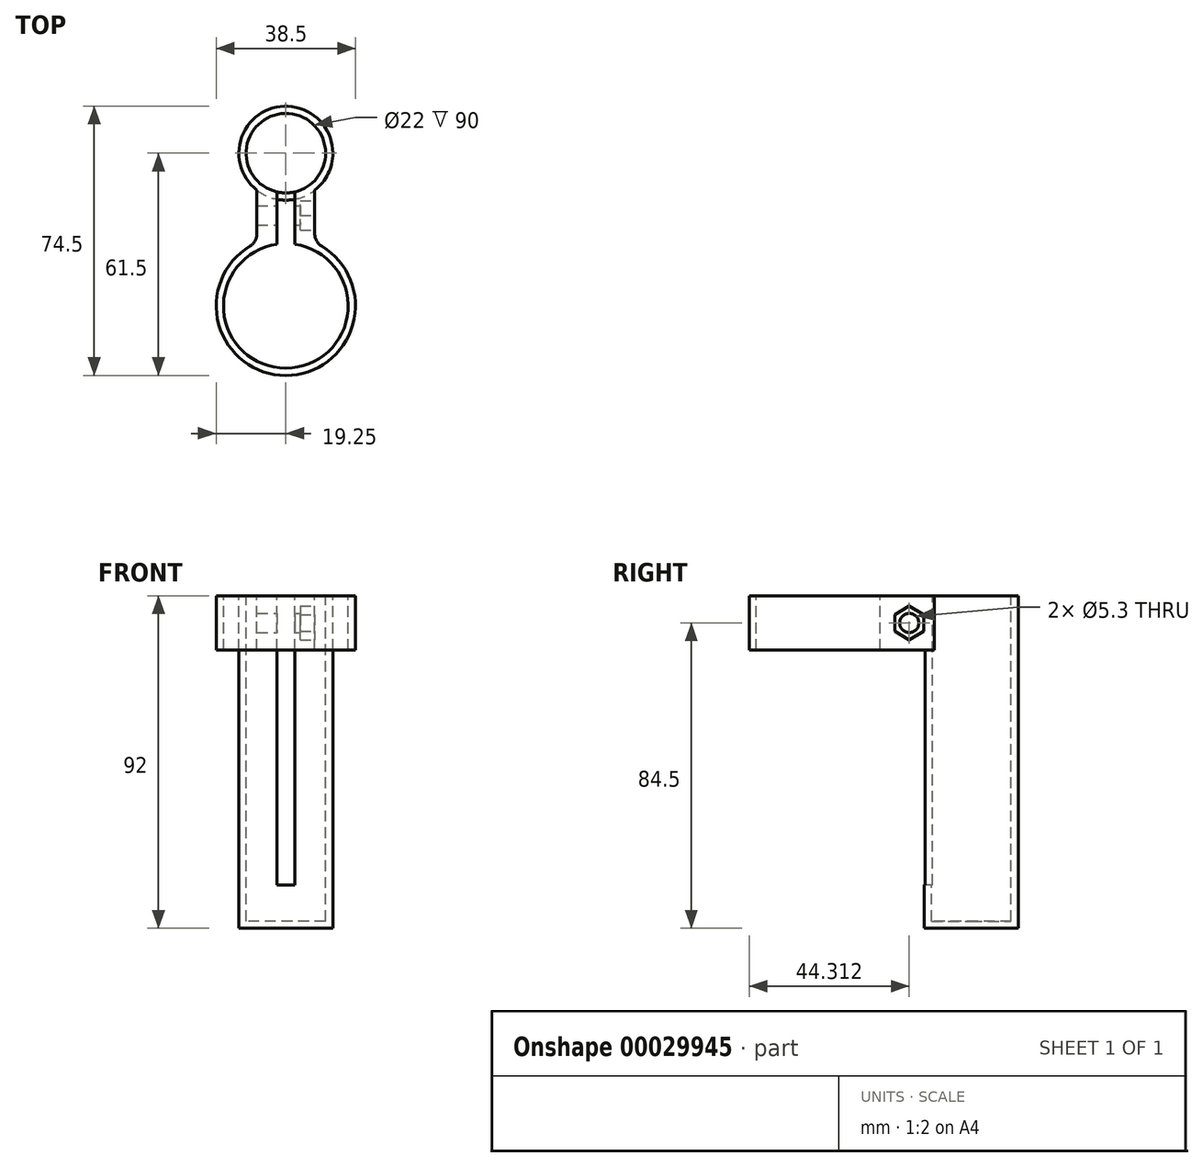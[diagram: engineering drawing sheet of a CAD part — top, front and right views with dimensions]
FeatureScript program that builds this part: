
annotation { "Feature Type Name" : "Feature", "Feature Type Description" : "" }
export const myFeature = defineFeature(function(context is Context, id is Id, definition is map)
    precondition{}
    {
        {
            var Q0;
            Q0=qCreatedBy(makeId("Top.planeOp"),FACE);
            var sketch = newSketch(context, id + "F0", { "sketchPlane" : qUnion([Q0])});
            skCircle(sketch, "E0", {"center": v(0, 0) * mm, "radius": 17.25 * mm});
            skCircle(sketch, "E1", {"center": v(0, 42.25) * mm, "radius": 11 * mm});
            skCircle(sketch, "E2", {"center": v(0, 42.25) * mm, "radius": 13 * mm});
            skCircle(sketch, "E3", {"center": v(0, 0) * mm, "radius": 19.25 * mm});
            skLineSegment(sketch, "E4", {"start": v(2.5, 31.54) * mm, "end": v(2.5, 17.07) * mm});
            skLineSegment(sketch, "E5", {"start": v(-2.5, 31.54) * mm, "end": v(-2.5, 17.07) * mm});
            skLineSegment(sketch, "E6", {"start": v(-8, 17.5) * mm, "end": v(-8, 32) * mm});
            skLineSegment(sketch, "E7", {"start": v(8, 32) * mm, "end": v(8, 17.5) * mm});
            skSolve(sketch);
        }
        {
            var Q0;
            {var subQ0=sQuery(id+"F0.wireOp",EDGE,"E6");Q0=makeQuery(id+"F0.imprint","IMPRINT",FACE,{"disambiguationData":[TD([[makeQuery(id+"F0.imprint","IMPRINT",EDGE,{"derivedFrom":subQ0}),-1.0]])]});}
            var Q1;
            {var subQ0=sQuery(id+"F0.wireOp",EDGE,"E7");Q1=makeQuery(id+"F0.imprint","IMPRINT",FACE,{"disambiguationData":[TD([[makeQuery(id+"F0.imprint","IMPRINT",EDGE,{"derivedFrom":subQ0}),-1.0]])]});}
            var Q2;
            {var subQ0=sQuery(id+"F0.wireOp",EDGE,"E6");Q2=makeQuery(id+"F0.imprint","IMPRINT",FACE,{"disambiguationData":[TD([[makeQuery(id+"F0.imprint","IMPRINT",EDGE,{"derivedFrom":subQ0}),-1.0]])]});}
            var Q3;
            {var subQ0=sQuery(id+"F0.wireOp",EDGE,"E7");Q3=makeQuery(id+"F0.imprint","IMPRINT",FACE,{"disambiguationData":[TD([[makeQuery(id+"F0.imprint","IMPRINT",EDGE,{"derivedFrom":subQ0}),-1.0]])]});}
            var Q4;
            {var subQ0=sQuery(id+"F0.wireOp",EDGE,"E4");var subQ3=sQuery(id+"F0.wireOp",EDGE,"E0");var subQ4=makeQuery(id+"F0.imprint","INTERSECT",VERTEX,{"derivedFrom":[subQ3,subQ0]});Q4=makeQuery(id+"F0.imprint","IMPRINT",FACE,{"disambiguationData":[TD([[makeQuery(id+"F0.imprint","IMPRINT",EDGE,{"disambiguationData":[TD([[subQ4,1.0]])],"derivedFrom":subQ3}),-1.0]])]});}
            var Q5;
            {var subQ0=sQuery(id+"F0.wireOp",EDGE,"E6");Q5=makeQuery(id+"F0.imprint","IMPRINT",FACE,{"disambiguationData":[TD([[makeQuery(id+"F0.imprint","IMPRINT",EDGE,{"derivedFrom":subQ0}),-1.0]])]});}
            var Q6;
            {var subQ0=sQuery(id+"F0.wireOp",EDGE,"E7");Q6=makeQuery(id+"F0.imprint","IMPRINT",FACE,{"disambiguationData":[TD([[makeQuery(id+"F0.imprint","IMPRINT",EDGE,{"derivedFrom":subQ0}),-1.0]])]});}
            var Q7;
            {var subQ0=sQuery(id+"F0.wireOp",EDGE,"E4");var subQ3=sQuery(id+"F0.wireOp",EDGE,"E0");var subQ4=makeQuery(id+"F0.imprint","INTERSECT",VERTEX,{"derivedFrom":[subQ3,subQ0]});Q7=makeQuery(id+"F0.imprint","IMPRINT",FACE,{"disambiguationData":[TD([[makeQuery(id+"F0.imprint","IMPRINT",EDGE,{"disambiguationData":[TD([[subQ4,1.0]])],"derivedFrom":subQ3}),-1.0]])]});}
            extrude(context, id + "F1", {"entities" : qUnion([Q0, Q1, Q2, Q3, Q4, Q5, Q6, Q7]), "oppositeDirection" : true, "depth" : 15 * mm});
        }
        {
            var Q0;
            {var subQ0=sQuery(id+"F0.wireOp",EDGE,"E5");var subQ3=sQuery(id+"F0.wireOp",EDGE,"E1");var subQ4=makeQuery(id+"F0.imprint","INTERSECT",VERTEX,{"derivedFrom":[subQ3,subQ0]});Q0=makeQuery(id+"F0.imprint","IMPRINT",FACE,{"disambiguationData":[TD([[makeQuery(id+"F0.imprint","IMPRINT",EDGE,{"disambiguationData":[TD([[subQ4,1.0]])],"derivedFrom":subQ3}),-1.0]])]});}
            var Q1;
            {var subQ0=sQuery(id+"F0.wireOp",EDGE,"E1");var subQ4=makeQuery(id+"F0.imprint","INTERSECT",VERTEX,{"derivedFrom":[subQ0,sQuery(id+"F0.wireOp",EDGE,"E5")]});Q1=makeQuery(id+"F0.imprint","IMPRINT",FACE,{"disambiguationData":[TD([[makeQuery(id+"F0.imprint","IMPRINT",EDGE,{"disambiguationData":[TD([[subQ4,1.0]])],"derivedFrom":subQ0}),1.0]])]});}
            var Q2;
            {var subQ3=sQuery(id+"F0.wireOp",EDGE,"E1");var subQ5=sQuery(id+"F0.wireOp",EDGE,"E4");var subQ7=makeQuery(id+"F0.imprint","INTERSECT",VERTEX,{"derivedFrom":[subQ3,subQ5]});Q2=makeQuery(id+"F0.imprint","IMPRINT",FACE,{"disambiguationData":[TD([[makeQuery(id+"F0.imprint","IMPRINT",EDGE,{"disambiguationData":[TD([[subQ7,1.0]])],"derivedFrom":subQ3}),-1.0]])]});}
            var Q3;
            {var subQ3=sQuery(id+"F0.wireOp",EDGE,"E1");var subQ5=sQuery(id+"F0.wireOp",EDGE,"b73e8383-4520-4388-ab81-a26b702ea739");var subQ7=makeQuery(id+"F0.imprint","INTERSECT",VERTEX,{"derivedFrom":[subQ3,subQ5]});Q3=makeQuery(id+"F0.imprint","IMPRINT",FACE,{"disambiguationData":[TD([[makeQuery(id+"F0.imprint","IMPRINT",EDGE,{"disambiguationData":[TD([[subQ7,1.0]])],"derivedFrom":subQ3}),-1.0]])]});}
            var Q4;
            {var subQ3=sQuery(id+"F0.wireOp",EDGE,"E1");var subQ5=sQuery(id+"F0.wireOp",EDGE,"E4");var subQ7=makeQuery(id+"F0.imprint","INTERSECT",VERTEX,{"derivedFrom":[subQ3,subQ5]});Q4=makeQuery(id+"F0.imprint","IMPRINT",FACE,{"disambiguationData":[TD([[makeQuery(id+"F0.imprint","IMPRINT",EDGE,{"disambiguationData":[TD([[subQ7,-1.0]])],"derivedFrom":subQ3}),-1.0]])]});}
            extrude(context, id + "F2", {"entities" : qUnion([Q0, Q1, Q2, Q3, Q4]), "operationType" : NewBodyOperationType.ADD, "oppositeDirection" : true, "depth" : 92 * mm});
        }
        {
            var Q0;
            {var subQ0=sQuery(id+"F0.wireOp",EDGE,"E1");var subQ4=makeQuery(id+"F0.imprint","INTERSECT",VERTEX,{"derivedFrom":[subQ0,sQuery(id+"F0.wireOp",EDGE,"E5")]});Q0=makeQuery(id+"F0.imprint","IMPRINT",FACE,{"disambiguationData":[TD([[makeQuery(id+"F0.imprint","IMPRINT",EDGE,{"disambiguationData":[TD([[subQ4,1.0]])],"derivedFrom":subQ0}),1.0]])]});}
            extrude(context, id + "F3", {"entities" : qUnion([Q0]), "operationType" : NewBodyOperationType.REMOVE, "oppositeDirection" : true, "depth" : 90 * mm});
        }
        {
            var Q0;
            {var subQ3=sQuery(id+"F0.wireOp",EDGE,"E1");var subQ5=sQuery(id+"F0.wireOp",EDGE,"E4");var subQ7=makeQuery(id+"F0.imprint","INTERSECT",VERTEX,{"derivedFrom":[subQ3,subQ5]});Q0=makeQuery(id+"F0.imprint","IMPRINT",FACE,{"disambiguationData":[TD([[makeQuery(id+"F0.imprint","IMPRINT",EDGE,{"disambiguationData":[TD([[subQ7,1.0]])],"derivedFrom":subQ3}),-1.0]])]});}
            extrude(context, id + "F4", {"entities" : qUnion([Q0]), "operationType" : NewBodyOperationType.REMOVE, "oppositeDirection" : true, "depth" : 80 * mm});
        }
        {
            var Q0;
            Q0=makeQuery(id+"F1.opExtrude","SWEPT_EDGE",EDGE,{"disambiguationData":[OSD([sQuery(id+"F0.wireOp",EDGE,"E3"),sQuery(id+"F0.wireOp",EDGE,"b73e8383-4520-4388-ab81-a26b702ea739")])]});
            var Q1;
            Q1=makeQuery(id+"F1.opExtrude","SWEPT_EDGE",EDGE,{"disambiguationData":[OSD([sQuery(id+"F0.wireOp",EDGE,"E2"),sQuery(id+"F0.wireOp",EDGE,"386e1edd-4529-49db-bf96-07d6fa47e71e")])]});
            var Q2;
            Q2=makeQuery(id+"F1.opExtrude","SWEPT_EDGE",EDGE,{"disambiguationData":[OSD([sQuery(id+"F0.wireOp",EDGE,"E3"),sQuery(id+"F0.wireOp",EDGE,"386e1edd-4529-49db-bf96-07d6fa47e71e")])]});
            var Q3;
            Q3=makeQuery(id+"F1.opExtrude","SWEPT_EDGE",EDGE,{"disambiguationData":[OSD([sQuery(id+"F0.wireOp",EDGE,"E2"),sQuery(id+"F0.wireOp",EDGE,"b73e8383-4520-4388-ab81-a26b702ea739")])]});
            var Q4;
            {var subQ0=sQuery(id+"F0.wireOp",EDGE,"E2");Q4=makeQuery(id+"F1.opExtrude","CAP_EDGE",EDGE,{"disambiguationData":[OSD([subQ0]),TDD([makeQuery(id+"F0.imprint","IMPRINT",EDGE,{"disambiguationData":[TD([[makeQuery(id+"F0.imprint","INTERSECT",VERTEX,{"derivedFrom":[subQ0,sQuery(id+"F0.wireOp",EDGE,"386e1edd-4529-49db-bf96-07d6fa47e71e")]}),1.0]])],"derivedFrom":subQ0})])],"isStart":false});}
            var Q5;
            {var subQ0=sQuery(id+"F0.wireOp",EDGE,"E2");Q5=makeQuery(id+"F1.opExtrude","CAP_EDGE",EDGE,{"disambiguationData":[OSD([subQ0]),TDD([makeQuery(id+"F0.imprint","IMPRINT",EDGE,{"disambiguationData":[TD([[makeQuery(id+"F0.imprint","INTERSECT",VERTEX,{"derivedFrom":[subQ0,sQuery(id+"F0.wireOp",EDGE,"b73e8383-4520-4388-ab81-a26b702ea739")]}),-1.0]])],"derivedFrom":subQ0})])],"isStart":false});}
            fillet(context, id + "F5", {"entities" : qUnion([Q0, Q1, Q2, Q3, Q4, Q5]), "radius" : 4 * mm, "tangentPropagation" : true, "allowEdgeOverflow" : false});
        }
        {
            var Q0;
            Q0=makeQuery(id+"F1.opExtrude","SWEPT_FACE",FACE,{"disambiguationData":[OSD([sQuery(id+"F0.wireOp",EDGE,"E7")])]});
            var sketch = newSketch(context, id + "F6", { "sketchPlane" : qUnion([Q0])});
            skLineSegment(sketch, "E8.rect.bottom", {"start": v(30.21, 0) * mm, "end": v(19.91, 0) * mm, "construction": true});
            skLineSegment(sketch, "E8.rect.top", {"start": v(30.21, -15) * mm, "end": v(19.91, -15) * mm, "construction": true});
            skLineSegment(sketch, "E8.rect.left", {"start": v(30.21, 0) * mm, "end": v(30.21, -15) * mm, "construction": true});
            skLineSegment(sketch, "E8.rect.right", {"start": v(19.91, 0) * mm, "end": v(19.91, -15) * mm, "construction": true});
            skPoint(sketch, "E8.rect.middle", {"position": v(25.06, -7.5) * mm});
            skCircle(sketch, "E9", {"center": v(25.06, -7.5) * mm, "radius": 2.65 * mm});
            skCircle(sketch, "E10.cCircle", {"center": v(25.06, -7.5) * mm, "radius": 4.05 * mm, "construction": true});
            skLineSegment(sketch, "E10.0", {"start": v(29.11, -5.16) * mm, "end": v(29.11, -9.84) * mm});
            skLineSegment(sketch, "E10.1", {"start": v(29.11, -9.84) * mm, "end": v(25.06, -12.18) * mm});
            skLineSegment(sketch, "E10.2", {"start": v(25.06, -12.18) * mm, "end": v(21.01, -9.84) * mm});
            skLineSegment(sketch, "E10.3", {"start": v(21.01, -9.84) * mm, "end": v(21.01, -5.16) * mm});
            skLineSegment(sketch, "E10.4", {"start": v(21.01, -5.16) * mm, "end": v(25.06, -2.82) * mm});
            skLineSegment(sketch, "E10.5", {"start": v(25.06, -2.82) * mm, "end": v(29.11, -5.16) * mm});
            skPoint(sketch, "E10.0.midPoint", {"position": v(29.11, -7.5) * mm});
            skSolve(sketch);
        }
        {
            var Q0;
            Q0=makeQuery(id+"F6.imprint","IMPRINT",FACE,{"disambiguationData":[TD([[makeQuery(id+"F6.imprint","IMPRINT",EDGE,{"derivedFrom":sQuery(id+"F6.wireOp",EDGE,"E9")}),-1.0]])]});
            extrude(context, id + "F7", {"entities" : qUnion([Q0]), "operationType" : NewBodyOperationType.REMOVE, "oppositeDirection" : true, "depth" : 4 * mm});
        }
        {
            var Q0;
            Q0=makeQuery(id+"F6.imprint","IMPRINT",FACE,{"disambiguationData":[TD([[makeQuery(id+"F6.imprint","IMPRINT",EDGE,{"derivedFrom":sQuery(id+"F6.wireOp",EDGE,"E9")}),1.0]])]});
            extrude(context, id + "F8", {"entities" : qUnion([Q0]), "operationType" : NewBodyOperationType.REMOVE, "endBound" : BoundingType.THROUGH_ALL, "oppositeDirection" : true, "depth" : 25 * mm});
        }
    });
